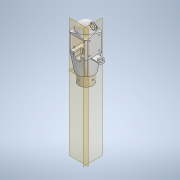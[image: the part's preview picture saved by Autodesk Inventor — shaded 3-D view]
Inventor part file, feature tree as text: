
AUTODESK INVENTOR PART (.ipt)
format: ipt  version: 2022.3 (Build 263350000, 350)  size: 744,448 bytes
history: native  units: mm
features: sketch x21, extrude x16, thicken_offset x7, fillet x5, plane x4, hole x4, mirror x3, revolve x2, projected_geometry x2, loft x1, other x1
ambient origin geometry x8: Origin, YZ Plane, XZ Plane, XY Plane, X Axis, Y Axis, Z Axis, Center Point
bodies: Solid1 (feature_tree)
feature tree (66):
  extrude  "Extrusion1"  Depth=4.0mm
  revolve  "Revolution1"  [1 undecoded]
  plane  "Work Plane1"
  extrude  "Extrusion2"  Depth=100.0mm
  extrude  "Extrusion3"  Depth=150.0mm
  plane  "Work Plane2"
  sketch  "Sketch5"  dims[d12=100.0mm d13=90.0deg]
  fillet  "Fillet1"  Radius=4.0mm
  loft  "Loft1"
  extrude  "Extrusion4"  Depth=5.0mm
  sketch  "Sketch11"  dims[d16=65.0mm d17=65.0mm]
  extrude  "Extrusion7"  Depth=65.0mm
  extrude  "Extrusion8"  Depth=15.0mm
  extrude  "Extrusion9"  Depth=10.0mm TaperAngle=0.0deg
  hole  "Hole2"  [1 undecoded]
  extrude  "Extrusion10"  Depth=50.0mm
  revolve  "Revolution2"  Angle=90.0deg
  fillet  "Fillet3"  [1 undecoded]
  extrude  "Extrusion14"  Depth=5.0mm
  sketch  "Sketch22"  dims[d33=100.0mm d34=0.0mm d54=5.0mm]
  extrude  "Extrusion15"  Depth=5.0mm TaperAngle=0.0deg
  extrude  "Extrusion16"  Depth=45.0mm
  plane  "Work Plane3"
  plane  "Work Plane4"
  sketch  "Sketch23"  dims[d55=4.5mm d56=5.0mm d57=0.0mm]
  sketch  "Sketch24"  dims[d58=48.0mm d59=0.0mm d60=45.0mm]
  hole  "Hole5"  [1 undecoded]
  hole  "Hole6"  [1 undecoded]
  mirror  "Mirror1"
  mirror  "Mirror2"
  thicken_offset  "Thicken1"
  thicken_offset  "Thicken2"
  thicken_offset  "Thicken3"
  thicken_offset  "Thicken4"
  thicken_offset  "Thicken5"
  extrude  "Extrusion17"  Depth=2.0mm TaperAngle=0.0deg
  fillet  "Fillet4"  Radius=26.0mm
  extrude  "Extrusion18"  TaperAngle=90.0deg  [1 undecoded]
  sketch  "Sketch27"  dims[d66=3.4mm d67=6.0mm d68=5.9mm d69=2.0mm d70=90.0deg d71=5.0mm d72=0.0mm d73=3.0mm d74=0.0mm d75=26.0mm]
  thicken_offset  "Thicken6"
  extrude  "Extrusion20"  TaperAngle=0.0deg  [1 undecoded]
  fillet  "Fillet6"  Radius=10.0mm
  extrude  "Extrusion21"  Depth=10.0mm TaperAngle=0.0deg
  thicken_offset  "Thicken7"
  hole  "Hole7"  [1 undecoded]
  mirror  "Mirror3"
  extrude  "Extrusion22"  Depth=2.0mm
  fillet  "Fillet7"  Radius=42.0mm
  sketch  "Sketch1"  dims[d0=80.0mm d1=4.0mm]
  sketch  "Sketch2"  dims[d2=40.0mm d3=0.0mm d4=88.0mm]
  sketch  "Sketch3"  dims[d5=50.0mm d8=100.0mm]
  sketch  "Sketch4"  dims[d9=25.0mm d10=150.0mm d11=4.0mm]
  other  "Edges1"
  sketch  "Sketch7"  dims[d14=-52.5mm d15=5.0mm]
  projected_geometry  "Projected Loop2"
  sketch  "Sketch12"  dims[d18=5.0mm d19=15.0mm]
  sketch  "Sketch13"  dims[d20=10.0mm d21=5.0mm d22=0.0mm]
  sketch  "Sketch14"  dims[d23=52.0mm d24=52.0mm]
  sketch  "Sketch15"  dims[d25=5.0mm d26=0.0mm d27=50.0mm]
  sketch  "Sketch21"  dims[d28=5.0mm d29=0.0mm d30=90.0deg d31=0.0mm d32=90.0deg]
  sketch  "Sketch25"  dims[d61=22.4mm d62=42.0mm d63=0.0mm]
  sketch  "Sketch26"  dims[d64=31.0mm d65=31.0mm]
  projected_geometry  "Projected Loop3"
  sketch  "Sketch29"  dims[d76=26.0mm d77=90.0deg]
  sketch  "Sketch30"  dims[d78=10.0mm d79=0.0mm d143=10.0mm d144=0.0mm]
  sketch  "Sketch31"  dims[d145=30.0mm d146=10.0mm d147=0.0mm d148=30.0mm d149=0.0mm d150=21.0mm d151=21.0mm d152=3.4mm d153=6.0mm d154=4.1mm d155=5.1mm d156=90.0deg d157=1.2mm d158=0.0mm d159=3.4mm d160=6.0mm d161=4.1mm d162=5.1mm d163=90.0deg d164=1.2mm d165=0.0mm d166=42.0mm d167=0.5mm d168=0.5mm d169=0.5mm d170=0.5mm d171=1.0mm d172=1.0mm d173=1.0mm d174=1.0mm d175=1.0mm d176=1.0mm d177=10.0mm d178=10.0mm d179=12.0mm d180=12.0mm d181=14.0mm d182=3.0mm d183=2.5mm d184=2.5mm d185=0.0mm d186=0.0mm d187=2.0mm d188=17.0mm d189=5.0mm d190=27.0mm d191=5.0mm d192=20.0mm d193=10.0mm d194=0.0mm d195=0.0mm d196=20.0mm d197=14.0mm d205=18.0mm d206=44.0mm d207=15.0mm d208=10.0mm d209=15.0mm d210=0.0mm d211=2.0mm d212=41.8mm d213=30.0mm d214=0.0mm d215=30.0mm d216=40.0mm d217=3.4mm d218=6.0mm d219=4.1mm d220=5.1mm d221=90.0deg d222=1.2mm d223=0.0mm d224=3.0mm d225=3.0mm d226=0.0mm d227=0.0mm d228=2.0mm d125=0.872665mm d126=0.872665mm d131=1.0mm d132=1.0mm d133=1.0mm d134=0.15mm d135=0.25mm d136=0.375mm d137=14.3117mm d138=0.75mm d139=20.594885mm d140=0.0625mm d141=0.75mm d142=0.375mm d198=0.5mm d199=0.872665mm d200=0.5mm d201=0.872665mm d229=0.872665mm]
note: 8 required parameter values undecoded (feature->parameter linkage not recoverable at this tier; creation-order binding heuristic only, values carry confidence <= 0.55)